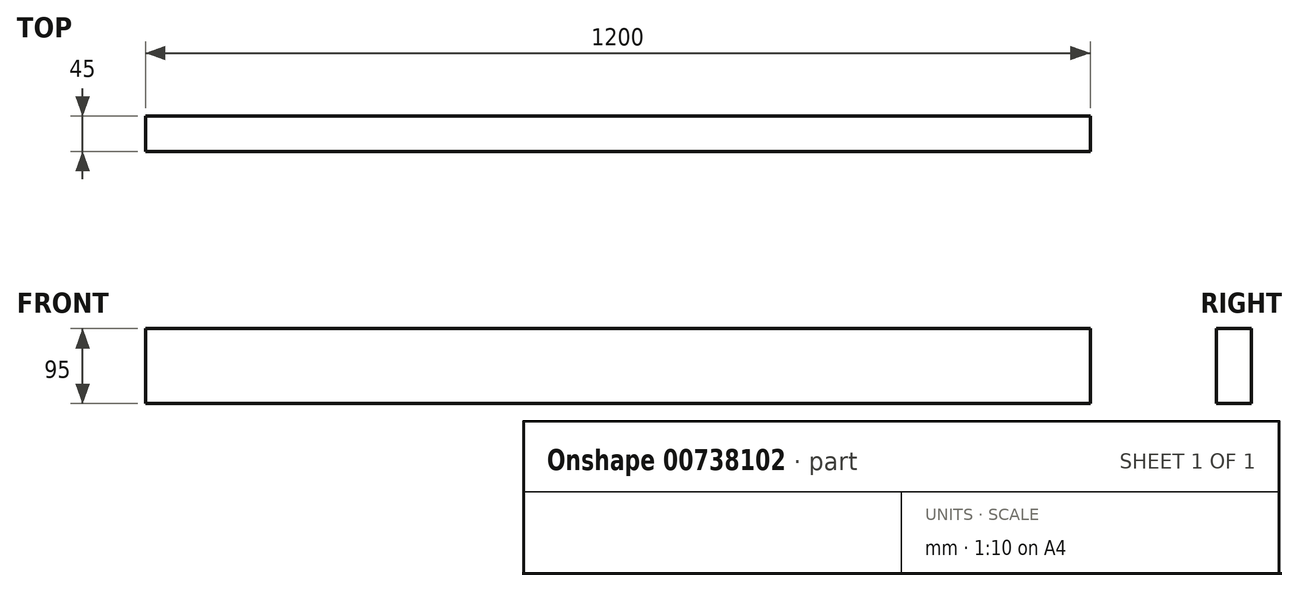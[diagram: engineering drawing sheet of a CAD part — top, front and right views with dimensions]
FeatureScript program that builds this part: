
annotation { "Feature Type Name" : "Feature", "Feature Type Description" : "" }
export const myFeature = defineFeature(function(context is Context, id is Id, definition is map)
    precondition{}
    {
        {
            var Q0;
            Q0=qCreatedBy(makeId("Front.planeOp"),FACE);
            var sketch = newSketch(context, id + "F0", { "sketchPlane" : qUnion([Q0])});
            skLineSegment(sketch, "E0.bottom", {"start": v(-277.55, 64.47) * mm, "end": v(922.45, 64.47) * mm});
            skLineSegment(sketch, "E0.top", {"start": v(-277.55, -30.53) * mm, "end": v(922.45, -30.53) * mm});
            skLineSegment(sketch, "E0.left", {"start": v(-277.55, 64.47) * mm, "end": v(-277.55, -30.53) * mm});
            skLineSegment(sketch, "E0.right", {"start": v(922.45, 64.47) * mm, "end": v(922.45, -30.53) * mm});
            skSolve(sketch);
        }
        {
            var Q0;
            Q0=makeQuery(id+"F0.imprint","IMPRINT",FACE,{"disambiguationData":[TD([[makeQuery(id+"F0.imprint","IMPRINT",EDGE,{"derivedFrom":sQuery(id+"F0.wireOp",EDGE,"E0.bottom")}),-1.0]])]});
            extrude(context, id + "F1", {"entities" : qUnion([Q0]), "depth" : 45 * mm, "offsetDistance" : 25 * mm});
        }
    });
